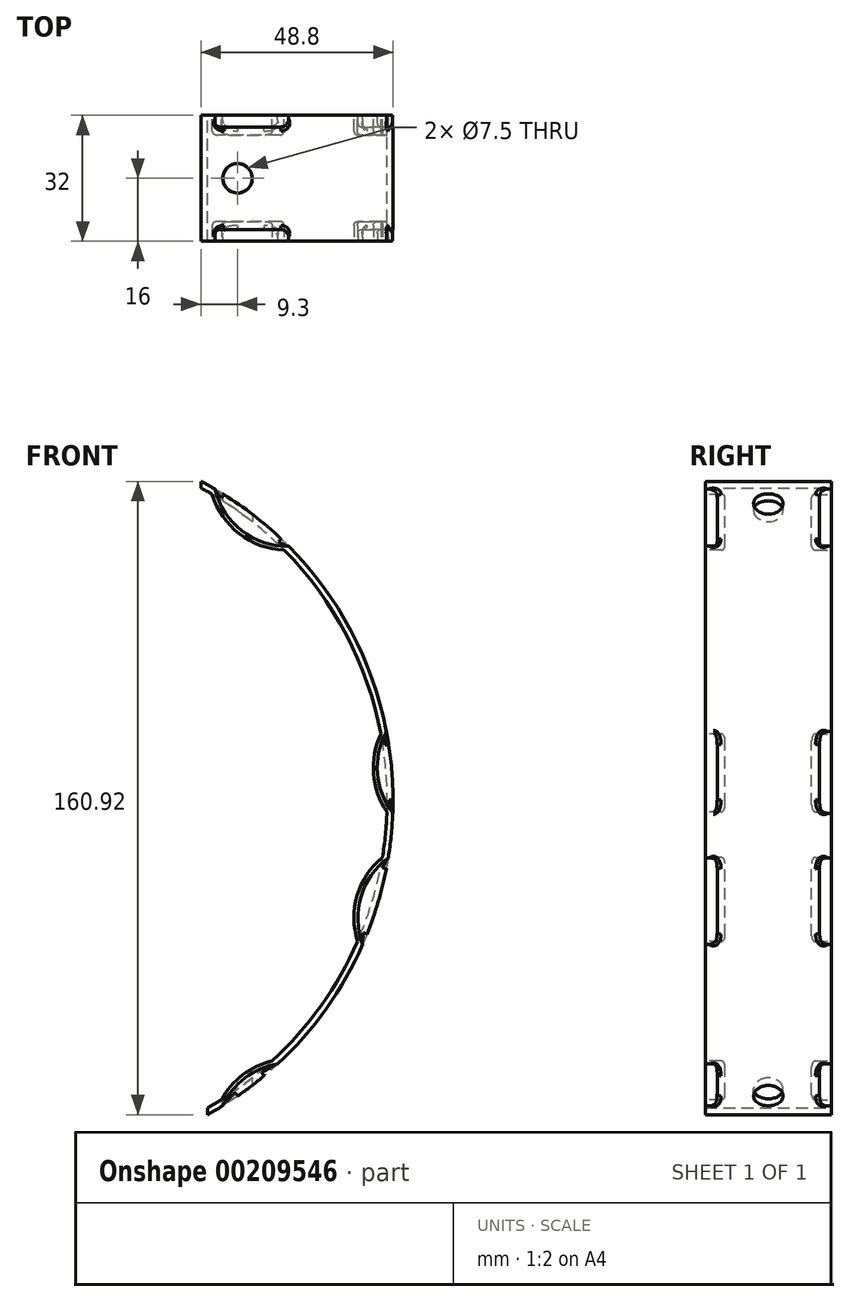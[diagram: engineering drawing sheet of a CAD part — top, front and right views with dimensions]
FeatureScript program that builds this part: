
annotation { "Feature Type Name" : "Feature", "Feature Type Description" : "" }
export const myFeature = defineFeature(function(context is Context, id is Id, definition is map)
    precondition{}
    {
        {
            var Q0;
            Q0=qCreatedBy(makeId("Front.planeOp"),FACE);
            var sketch = newSketch(context, id + "F0", { "sketchPlane" : qUnion([Q0])});
            skArc(sketch, "E0", {"start": v(44.4, -78.28) * mm, "mid": v(90, 0.97) * mm, "end": v(42.7, 79.22) * mm});
            skLineSegment(sketch, "E1", {"start": v(50.5, 74.5) * mm, "end": v(50.5, -74.5) * mm, "construction": true});
            skLineSegment(sketch, "E2", {"start": v(0, 0) * mm, "end": v(50.5, 0) * mm, "construction": true});
            skLineSegment(sketch, "E3", {"start": v(0, 0) * mm, "end": v(40, 0) * mm, "construction": true});
            skLineSegment(sketch, "E4", {"start": v(40, 0) * mm, "end": v(64.7, 83.42) * mm, "construction": true});
            skLineSegment(sketch, "E5", {"start": v(40, 0) * mm, "end": v(65.42, -85.81) * mm, "construction": true});
            skLineSegment(sketch, "E6", {"start": v(40, 0) * mm, "end": v(101.57, -30.03) * mm, "construction": true});
            skLineSegment(sketch, "E7", {"start": v(40, 0) * mm, "end": v(106.5, 8.17) * mm, "construction": true});
            skArc(sketch, "E8", {"start": v(88.43, 16.74) * mm, "mid": v(86.56, 6.64) * mm, "end": v(89.95, -3.06) * mm});
            skArc(sketch, "E9", {"start": v(45.57, 77.6) * mm, "mid": v(52.45, 67.61) * mm, "end": v(63.84, 63.44) * mm});
            skArc(sketch, "E10", {"start": v(88.8, -14.63) * mm, "mid": v(82.39, -24.36) * mm, "end": v(82.48, -36) * mm});
            skArc(sketch, "E11", {"start": v(60.8, -66.35) * mm, "mid": v(53.3, -69.9) * mm, "end": v(47.88, -76.2) * mm});
            skArc(sketch, "E12", {"start": v(44.4, -80) * mm, "mid": v(91.5, 0.97) * mm, "end": v(42.7, 80.92) * mm});
            skLineSegment(sketch, "E13", {"start": v(42.7, 79.22) * mm, "end": v(42.7, 80.92) * mm});
            skPoint(sketch, "E14", {"position": v(47.72, -76.3) * mm});
            skLineSegment(sketch, "E15", {"start": v(44.4, -78.28) * mm, "end": v(44.4, -80) * mm});
            skPoint(sketch, "E16.start.orphan", {"position": v(31.58, -84.28) * mm});
            skSolve(sketch);
        }
        {
            var Q0;
            Q0=makeQuery(id+"F0.imprint","IMPRINT",FACE,{"disambiguationData":[TD([[makeQuery(id+"F0.imprint","IMPRINT",EDGE,{"derivedFrom":sQuery(id+"F0.wireOp",EDGE,"E12")}),1.0]])]});
            extrude(context, id + "F1", {"entities" : qUnion([Q0]), "depth" : 32 * mm});
        }
        {
            var Q0;
            {var subQ0=sQuery(id+"F0.wireOp",EDGE,"E9");Q0=makeQuery(id+"F0.imprint","IMPRINT",FACE,{"disambiguationData":[TD([[makeQuery(id+"F0.imprint","IMPRINT",EDGE,{"derivedFrom":subQ0}),1.0]])]});}
            var Q1;
            {var subQ0=sQuery(id+"F0.wireOp",EDGE,"E8");Q1=makeQuery(id+"F0.imprint","IMPRINT",FACE,{"disambiguationData":[TD([[makeQuery(id+"F0.imprint","IMPRINT",EDGE,{"derivedFrom":subQ0}),1.0]])]});}
            var Q2;
            {var subQ0=sQuery(id+"F0.wireOp",EDGE,"E10");Q2=makeQuery(id+"F0.imprint","IMPRINT",FACE,{"disambiguationData":[TD([[makeQuery(id+"F0.imprint","IMPRINT",EDGE,{"derivedFrom":subQ0}),1.0]])]});}
            var Q3;
            {var subQ0=sQuery(id+"F0.wireOp",EDGE,"E11");Q3=makeQuery(id+"F0.imprint","IMPRINT",FACE,{"disambiguationData":[TD([[makeQuery(id+"F0.imprint","IMPRINT",EDGE,{"derivedFrom":subQ0}),1.0]])]});}
            extrude(context, id + "F2", {"entities" : qUnion([Q0, Q1, Q2, Q3]), "operationType" : NewBodyOperationType.ADD, "depth" : 5 * mm});
        }
        {
            var Q0;
            Q0=makeQuery(id+"F1.opExtrude","CAP_FACE",FACE,{"disambiguationData":[OSD([sQuery(id+"F0.wireOp",EDGE,"E0"),sQuery(id+"F0.wireOp",EDGE,"E12"),sQuery(id+"F0.wireOp",EDGE,"E13"),sQuery(id+"F0.wireOp",EDGE,"E16")])],"isStart":false});
            var sketch = newSketch(context, id + "F3", { "sketchPlane" : qUnion([Q0])});
            skArc(sketch, "E17.0", {"start": v(45.57, 77.6) * mm, "mid": v(52.45, 67.61) * mm, "end": v(63.84, 63.44) * mm});
            skArc(sketch, "E18.0", {"start": v(44.4, -78.28) * mm, "mid": v(90, 0.97) * mm, "end": v(42.7, 79.22) * mm});
            skArc(sketch, "E19.0", {"start": v(88.43, 16.74) * mm, "mid": v(86.56, 6.64) * mm, "end": v(89.95, -3.06) * mm});
            skArc(sketch, "E20.0", {"start": v(88.8, -14.63) * mm, "mid": v(82.39, -24.36) * mm, "end": v(82.48, -36) * mm});
            skArc(sketch, "E21.0", {"start": v(60.8, -66.35) * mm, "mid": v(53.3, -69.9) * mm, "end": v(47.88, -76.2) * mm});
            skSolve(sketch);
        }
        {
            var Q0;
            Q0 = qSketchRegion(id + "F3", true);
            extrude(context, id + "F4", {"entities" : qUnion([Q0]), "operationType" : NewBodyOperationType.ADD, "oppositeDirection" : true, "depth" : 5 * mm});
        }
        {
            var Q0;
            {var subQ0=sQuery(id+"F3.wireOp",EDGE,"E18.0");Q0=makeQuery(id+"F4.boolean.opBoolean","MERGE",FACE,{"derivedFrom":[makeQuery(id+"F1.opExtrude","CAP_FACE",FACE,{"disambiguationData":[OSD([sQuery(id+"F0.wireOp",EDGE,"E0"),sQuery(id+"F0.wireOp",EDGE,"E12"),sQuery(id+"F0.wireOp",EDGE,"E13"),sQuery(id+"F0.wireOp",EDGE,"E16")])],"isStart":false}),makeQuery(id+"F4.opExtrude","CAP_FACE",FACE,{"disambiguationData":[OSD([sQuery(id+"F3.wireOp",EDGE,"E17.0"),subQ0])],"isStart":true}),makeQuery(id+"F4.opExtrude","CAP_FACE",FACE,{"disambiguationData":[OSD([subQ0,sQuery(id+"F3.wireOp",EDGE,"E21.0")])],"isStart":true}),makeQuery(id+"F4.opExtrude","CAP_FACE",FACE,{"disambiguationData":[OSD([subQ0,sQuery(id+"F3.wireOp",EDGE,"E20.0")])],"isStart":true}),makeQuery(id+"F4.opExtrude","CAP_FACE",FACE,{"disambiguationData":[OSD([subQ0,sQuery(id+"F3.wireOp",EDGE,"E19.0")])],"isStart":true})]});}
            var sketch = newSketch(context, id + "F5", { "sketchPlane" : qUnion([Q0])});
            skArc(sketch, "E22.0", {"start": v(45.57, 77.6) * mm, "mid": v(52.45, 67.61) * mm, "end": v(63.84, 63.44) * mm});
            skCircle(sketch, "E23", {"center": v(64.7, 83.42) * mm, "radius": 19 * mm});
            skArc(sketch, "E24.0", {"start": v(44.4, -80) * mm, "mid": v(91.5, 0.97) * mm, "end": v(42.7, 80.92) * mm});
            skArc(sketch, "E25.0", {"start": v(88.43, 16.74) * mm, "mid": v(86.56, 6.64) * mm, "end": v(89.95, -3.06) * mm});
            skCircle(sketch, "E26", {"center": v(106.5, 8.17) * mm, "radius": 19 * mm});
            skArc(sketch, "E27.0", {"start": v(88.8, -14.63) * mm, "mid": v(82.39, -24.36) * mm, "end": v(82.48, -36) * mm});
            skArc(sketch, "E28.0", {"start": v(60.8, -66.35) * mm, "mid": v(53.3, -69.9) * mm, "end": v(47.88, -76.2) * mm});
            skCircle(sketch, "E29", {"center": v(101.57, -30.03) * mm, "radius": 19 * mm});
            skCircle(sketch, "E30", {"center": v(65.42, -85.81) * mm, "radius": 19 * mm});
            skSolve(sketch);
        }
        {
            var Q0;
            Q0 = qSketchRegion(id + "F5", true);
            extrude(context, id + "F6", {"entities" : qUnion([Q0]), "operationType" : NewBodyOperationType.REMOVE, "oppositeDirection" : true, "depth" : 3 * mm});
        }
        {
            var Q0;
            Q0=makeQuery(id+"F4.opExtrude","CAP_EDGE",EDGE,{"disambiguationData":[OSD([sQuery(id+"F3.wireOp",EDGE,"E21.0")])],"isStart":false});
            var Q1;
            Q1=makeQuery(id+"F4.opExtrude","CAP_EDGE",EDGE,{"disambiguationData":[OSD([sQuery(id+"F3.wireOp",EDGE,"E19.0")])],"isStart":false});
            var Q2;
            Q2=makeQuery(id+"F4.opExtrude","CAP_EDGE",EDGE,{"disambiguationData":[OSD([sQuery(id+"F3.wireOp",EDGE,"E17.0")])],"isStart":false});
            var Q3;
            Q3=makeQuery(id+"F4.opExtrude","CAP_EDGE",EDGE,{"disambiguationData":[OSD([sQuery(id+"F3.wireOp",EDGE,"E20.0")])],"isStart":false});
            var Q4;
            Q4=makeQuery(id+"F2.opExtrude","CAP_EDGE",EDGE,{"disambiguationData":[OSD([sQuery(id+"F0.wireOp",EDGE,"E10")])],"isStart":false});
            var Q5;
            Q5=makeQuery(id+"F2.opExtrude","CAP_EDGE",EDGE,{"disambiguationData":[OSD([sQuery(id+"F0.wireOp",EDGE,"E8")])],"isStart":false});
            var Q6;
            Q6=makeQuery(id+"F2.opExtrude","CAP_EDGE",EDGE,{"disambiguationData":[OSD([sQuery(id+"F0.wireOp",EDGE,"E9")])],"isStart":false});
            var Q7;
            Q7=makeQuery(id+"F2.opExtrude","CAP_EDGE",EDGE,{"disambiguationData":[OSD([sQuery(id+"F0.wireOp",EDGE,"E11")])],"isStart":false});
            var Q8;
            Q8=makeQuery(id+"F6.boolean.opBoolean","COPY",EDGE,{"derivedFrom":makeQuery(id+"F6.opExtrude","CAP_EDGE",EDGE,{"disambiguationData":[OSD([sQuery(id+"F5.wireOp",EDGE,"E30")])],"isStart":false})});
            var Q9;
            Q9=makeQuery(id+"F6.boolean.opBoolean","INTERSECT",EDGE,{"derivedFrom":[makeQuery(id+"F1.opExtrude","SWEPT_FACE",FACE,{"disambiguationData":[OSD([sQuery(id+"F0.wireOp",EDGE,"E12")])]}),makeQuery(id+"F6.opExtrude","CAP_FACE",FACE,{"disambiguationData":[OSD([sQuery(id+"F5.wireOp",EDGE,"E30")])],"isStart":false})]});
            var Q10;
            Q10=makeQuery(id+"F6.boolean.opBoolean","INTERSECT",EDGE,{"derivedFrom":[makeQuery(id+"F1.opExtrude","SWEPT_FACE",FACE,{"disambiguationData":[OSD([sQuery(id+"F0.wireOp",EDGE,"E12")])]}),makeQuery(id+"F6.opExtrude","CAP_FACE",FACE,{"disambiguationData":[OSD([sQuery(id+"F5.wireOp",EDGE,"E29")])],"isStart":false})]});
            var Q11;
            Q11=makeQuery(id+"F6.boolean.opBoolean","COPY",EDGE,{"derivedFrom":makeQuery(id+"F6.opExtrude","CAP_EDGE",EDGE,{"disambiguationData":[OSD([sQuery(id+"F5.wireOp",EDGE,"E29")])],"isStart":false})});
            var Q12;
            Q12=makeQuery(id+"F6.boolean.opBoolean","COPY",EDGE,{"derivedFrom":makeQuery(id+"F6.opExtrude","CAP_EDGE",EDGE,{"disambiguationData":[OSD([sQuery(id+"F5.wireOp",EDGE,"E26")])],"isStart":false})});
            var Q13;
            Q13=makeQuery(id+"F6.boolean.opBoolean","COPY",EDGE,{"derivedFrom":makeQuery(id+"F6.opExtrude","CAP_EDGE",EDGE,{"disambiguationData":[OSD([sQuery(id+"F5.wireOp",EDGE,"E23")])],"isStart":false})});
            var Q14;
            Q14=makeQuery(id+"F6.boolean.opBoolean","INTERSECT",EDGE,{"derivedFrom":[makeQuery(id+"F1.opExtrude","SWEPT_FACE",FACE,{"disambiguationData":[OSD([sQuery(id+"F0.wireOp",EDGE,"E12")])]}),makeQuery(id+"F6.opExtrude","CAP_FACE",FACE,{"disambiguationData":[OSD([sQuery(id+"F5.wireOp",EDGE,"E23")])],"isStart":false})]});
            fillet(context, id + "F7", {"entities" : qUnion([Q0, Q1, Q2, Q3, Q4, Q5, Q6, Q7, Q8, Q9, Q10, Q11, Q12, Q13, Q14]), "radius" : 1 * mm, "tangentPropagation" : true, "allowEdgeOverflow" : false});
        }
        {
            var Q0;
            {var subQ0=sQuery(id+"F0.wireOp",EDGE,"E0");Q0=makeQuery(id+"F2.boolean.opBoolean","MERGE",FACE,{"derivedFrom":[makeQuery(id+"F1.opExtrude","CAP_FACE",FACE,{"disambiguationData":[OSD([subQ0,sQuery(id+"F0.wireOp",EDGE,"E12"),sQuery(id+"F0.wireOp",EDGE,"E13"),sQuery(id+"F0.wireOp",EDGE,"E16")])],"isStart":true}),makeQuery(id+"F2.opExtrude","CAP_FACE",FACE,{"disambiguationData":[OSD([subQ0,sQuery(id+"F0.wireOp",EDGE,"E11")])],"isStart":true}),makeQuery(id+"F2.opExtrude","CAP_FACE",FACE,{"disambiguationData":[OSD([subQ0,sQuery(id+"F0.wireOp",EDGE,"E10")])],"isStart":true}),makeQuery(id+"F2.opExtrude","CAP_FACE",FACE,{"disambiguationData":[OSD([subQ0,sQuery(id+"F0.wireOp",EDGE,"E8")])],"isStart":true}),makeQuery(id+"F2.opExtrude","CAP_FACE",FACE,{"disambiguationData":[OSD([subQ0,sQuery(id+"F0.wireOp",EDGE,"E9")])],"isStart":true})]});}
            var sketch = newSketch(context, id + "F8", { "sketchPlane" : qUnion([Q0])});
            skArc(sketch, "E31.0", {"start": v(-45.57, 77.6) * mm, "mid": v(-52.45, 67.61) * mm, "end": v(-63.84, 63.44) * mm});
            skArc(sketch, "E32.0", {"start": v(-44.4, -80) * mm, "mid": v(-91.5, 0.97) * mm, "end": v(-42.7, 80.92) * mm});
            skArc(sketch, "E33.0", {"start": v(-88.43, 16.74) * mm, "mid": v(-86.56, 6.64) * mm, "end": v(-89.95, -3.06) * mm});
            skArc(sketch, "E34.0", {"start": v(-88.8, -14.63) * mm, "mid": v(-82.39, -24.36) * mm, "end": v(-82.48, -36) * mm});
            skArc(sketch, "E35.0", {"start": v(-60.8, -66.35) * mm, "mid": v(-53.3, -69.9) * mm, "end": v(-47.88, -76.2) * mm});
            skCircle(sketch, "E36", {"center": v(-64.7, 83.42) * mm, "radius": 19 * mm});
            skCircle(sketch, "E37", {"center": v(-106.5, 8.17) * mm, "radius": 19 * mm});
            skCircle(sketch, "E38", {"center": v(-101.57, -30.03) * mm, "radius": 19 * mm});
            skCircle(sketch, "E39", {"center": v(-65.42, -85.81) * mm, "radius": 19 * mm});
            skSolve(sketch);
        }
        {
            var Q0;
            Q0 = qSketchRegion(id + "F8", true);
            extrude(context, id + "F9", {"entities" : qUnion([Q0]), "operationType" : NewBodyOperationType.REMOVE, "oppositeDirection" : true, "depth" : 3 * mm});
        }
        {
            var Q0;
            Q0=makeQuery(id+"F9.boolean.opBoolean","COPY",EDGE,{"derivedFrom":makeQuery(id+"F9.opExtrude","CAP_EDGE",EDGE,{"disambiguationData":[OSD([sQuery(id+"F8.wireOp",EDGE,"E37")])],"isStart":false})});
            var Q1;
            Q1=makeQuery(id+"F9.boolean.opBoolean","INTERSECT",EDGE,{"derivedFrom":[makeQuery(id+"F1.opExtrude","SWEPT_FACE",FACE,{"disambiguationData":[OSD([sQuery(id+"F0.wireOp",EDGE,"E12")])]}),makeQuery(id+"F9.opExtrude","CAP_FACE",FACE,{"disambiguationData":[OSD([sQuery(id+"F8.wireOp",EDGE,"E37")])],"isStart":false})]});
            var Q2;
            Q2=makeQuery(id+"F9.boolean.opBoolean","COPY",EDGE,{"derivedFrom":makeQuery(id+"F9.opExtrude","CAP_EDGE",EDGE,{"disambiguationData":[OSD([sQuery(id+"F8.wireOp",EDGE,"E37")])],"isStart":true})});
            var Q3;
            Q3=makeQuery(id+"F9.boolean.opBoolean","INTERSECT",EDGE,{"derivedFrom":[makeQuery(id+"F1.opExtrude","SWEPT_FACE",FACE,{"disambiguationData":[OSD([sQuery(id+"F0.wireOp",EDGE,"E12")])]}),makeQuery(id+"F9.opExtrude","CAP_FACE",FACE,{"disambiguationData":[OSD([sQuery(id+"F8.wireOp",EDGE,"E38")])],"isStart":false})]});
            var Q4;
            Q4=makeQuery(id+"F9.boolean.opBoolean","COPY",EDGE,{"derivedFrom":makeQuery(id+"F9.opExtrude","CAP_EDGE",EDGE,{"disambiguationData":[OSD([sQuery(id+"F8.wireOp",EDGE,"E38")])],"isStart":true})});
            var Q5;
            Q5=makeQuery(id+"F9.boolean.opBoolean","COPY",EDGE,{"derivedFrom":makeQuery(id+"F9.opExtrude","CAP_EDGE",EDGE,{"disambiguationData":[OSD([sQuery(id+"F8.wireOp",EDGE,"E38")])],"isStart":false})});
            var Q6;
            Q6=makeQuery(id+"F9.boolean.opBoolean","INTERSECT",EDGE,{"derivedFrom":[makeQuery(id+"F1.opExtrude","SWEPT_FACE",FACE,{"disambiguationData":[OSD([sQuery(id+"F0.wireOp",EDGE,"E12")])]}),makeQuery(id+"F9.opExtrude","CAP_FACE",FACE,{"disambiguationData":[OSD([sQuery(id+"F8.wireOp",EDGE,"E39")])],"isStart":false})]});
            var Q7;
            Q7=makeQuery(id+"F9.boolean.opBoolean","COPY",EDGE,{"derivedFrom":makeQuery(id+"F9.opExtrude","CAP_EDGE",EDGE,{"disambiguationData":[OSD([sQuery(id+"F8.wireOp",EDGE,"E39")])],"isStart":false})});
            var Q8;
            Q8=makeQuery(id+"F9.boolean.opBoolean","COPY",EDGE,{"derivedFrom":makeQuery(id+"F9.opExtrude","CAP_EDGE",EDGE,{"disambiguationData":[OSD([sQuery(id+"F8.wireOp",EDGE,"E39")])],"isStart":true})});
            var Q9;
            Q9=makeQuery(id+"F9.boolean.opBoolean","INTERSECT",EDGE,{"derivedFrom":[makeQuery(id+"F1.opExtrude","SWEPT_FACE",FACE,{"disambiguationData":[OSD([sQuery(id+"F0.wireOp",EDGE,"E12")])]}),makeQuery(id+"F9.opExtrude","CAP_FACE",FACE,{"disambiguationData":[OSD([sQuery(id+"F8.wireOp",EDGE,"E36")])],"isStart":false})]});
            var Q10;
            Q10=makeQuery(id+"F9.boolean.opBoolean","COPY",EDGE,{"derivedFrom":makeQuery(id+"F9.opExtrude","CAP_EDGE",EDGE,{"disambiguationData":[OSD([sQuery(id+"F8.wireOp",EDGE,"E36")])],"isStart":true})});
            var Q11;
            Q11=makeQuery(id+"F9.boolean.opBoolean","COPY",EDGE,{"derivedFrom":makeQuery(id+"F9.opExtrude","CAP_EDGE",EDGE,{"disambiguationData":[OSD([sQuery(id+"F8.wireOp",EDGE,"E36")])],"isStart":false})});
            var Q12;
            Q12=makeQuery(id+"F6.boolean.opBoolean","COPY",EDGE,{"derivedFrom":makeQuery(id+"F6.opExtrude","CAP_EDGE",EDGE,{"disambiguationData":[OSD([sQuery(id+"F5.wireOp",EDGE,"E23")])],"isStart":true})});
            var Q13;
            Q13=makeQuery(id+"F6.boolean.opBoolean","INTERSECT",EDGE,{"derivedFrom":[makeQuery(id+"F1.opExtrude","SWEPT_FACE",FACE,{"disambiguationData":[OSD([sQuery(id+"F0.wireOp",EDGE,"E12")])]}),makeQuery(id+"F6.opExtrude","CAP_FACE",FACE,{"disambiguationData":[OSD([sQuery(id+"F5.wireOp",EDGE,"E26")])],"isStart":false})]});
            var Q14;
            Q14=makeQuery(id+"F6.boolean.opBoolean","COPY",EDGE,{"derivedFrom":makeQuery(id+"F6.opExtrude","CAP_EDGE",EDGE,{"disambiguationData":[OSD([sQuery(id+"F5.wireOp",EDGE,"E29")])],"isStart":true})});
            var Q15;
            Q15=makeQuery(id+"F6.boolean.opBoolean","COPY",EDGE,{"derivedFrom":makeQuery(id+"F6.opExtrude","CAP_EDGE",EDGE,{"disambiguationData":[OSD([sQuery(id+"F5.wireOp",EDGE,"E30")])],"isStart":true})});
            fillet(context, id + "F10", {"entities" : qUnion([Q0, Q1, Q2, Q3, Q4, Q5, Q6, Q7, Q8, Q9, Q10, Q11, Q12, Q13, Q14, Q15]), "radius" : 1 * mm, "tangentPropagation" : true, "allowEdgeOverflow" : false});
        }
        {
            var Q0;
            Q0=qCreatedBy(makeId("Top.planeOp"),FACE);
            var sketch = newSketch(context, id + "F11", { "sketchPlane" : qUnion([Q0])});
            skLineSegment(sketch, "E40", {"start": v(52, 0) * mm, "end": v(52, -16) * mm, "construction": true});
            skPoint(sketch, "E41", {"position": v(52, -16) * mm});
            skLineSegment(sketch, "E42", {"start": v(52, 0) * mm, "end": v(0, 0) * mm, "construction": true});
            skSolve(sketch);
        }
        {
            var Q0;
            Q0=sQuery(id+"F11.wireOp",VERTEX,"E41");
            var Q1;
            Q1=makeQuery(id+"F1.opExtrude","SWEPT_BODY",BODY,{"disambiguationData":[OSD([sQuery(id+"F0.wireOp",EDGE,"E0"),sQuery(id+"F0.wireOp",EDGE,"E12"),sQuery(id+"F0.wireOp",EDGE,"E13"),sQuery(id+"F0.wireOp",EDGE,"E16")])]});
            hole(context, id + "F12", {"style" : HoleStyle.SIMPLE, "endStyle" : HoleEndStyle.THROUGH, "holeDiameter" : 7.5 * mm, "locations" : qUnion([Q0]), "scope" : qUnion([Q1]), "isTappedThrough" : true});
        }
        {
            var Q0;
            Q0=qCreatedBy(makeId("Top.planeOp"),FACE);
            var sketch = newSketch(context, id + "F13", { "sketchPlane" : qUnion([Q0])});
            skLineSegment(sketch, "E43", {"start": v(0, 0) * mm, "end": v(52, 0) * mm, "construction": true});
            skLineSegment(sketch, "E44", {"start": v(52, 0) * mm, "end": v(52, -16) * mm, "construction": true});
            skSolve(sketch);
        }
        {
            var Q0;
            Q0=sQuery(id+"F13.wireOp",VERTEX,"E44.end");
            var Q1;
            Q1=makeQuery(id+"F1.opExtrude","SWEPT_BODY",BODY,{"disambiguationData":[OSD([sQuery(id+"F0.wireOp",EDGE,"E0"),sQuery(id+"F0.wireOp",EDGE,"E12"),sQuery(id+"F0.wireOp",EDGE,"E13"),sQuery(id+"F0.wireOp",EDGE,"E16")])]});
            hole(context, id + "F14", {"style" : HoleStyle.SIMPLE, "endStyle" : HoleEndStyle.THROUGH, "oppositeDirection" : true, "holeDiameter" : 7.5 * mm, "locations" : qUnion([Q0]), "scope" : qUnion([Q1]), "isTappedThrough" : true});
        }
    });
